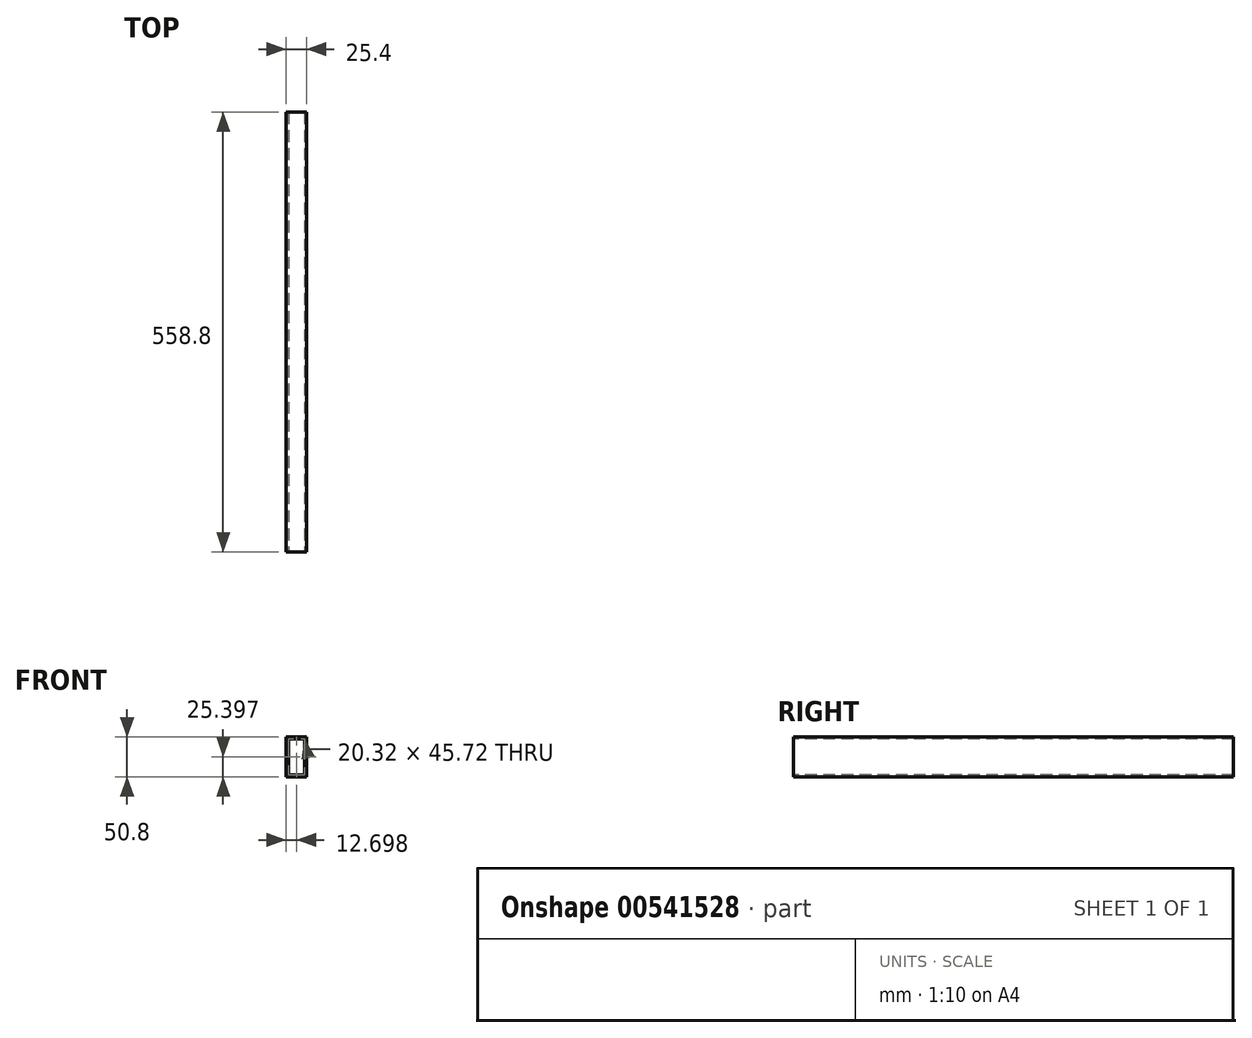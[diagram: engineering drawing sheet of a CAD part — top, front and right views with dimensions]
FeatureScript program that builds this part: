
annotation { "Feature Type Name" : "Feature", "Feature Type Description" : "" }
export const myFeature = defineFeature(function(context is Context, id is Id, definition is map)
    precondition{}
    {
        {
            var Q0;
            Q0=qCreatedBy(makeId("Front.planeOp"),FACE);
            var sketch = newSketch(context, id + "F0", { "sketchPlane" : qUnion([Q0])});
            skLineSegment(sketch, "E0.bottom", {"start": v(-22.94, 30.43) * mm, "end": v(2.46, 30.43) * mm});
            skLineSegment(sketch, "E0.top", {"start": v(-22.94, -20.37) * mm, "end": v(2.46, -20.37) * mm});
            skLineSegment(sketch, "E0.left", {"start": v(-22.94, 30.43) * mm, "end": v(-22.94, -20.37) * mm});
            skLineSegment(sketch, "E0.right", {"start": v(2.46, 30.43) * mm, "end": v(2.46, -20.37) * mm});
            skSolve(sketch);
        }
        {
            var Q0;
            Q0=qSketchRegion(id+"F0",true);
            extrude(context, id + "F1", {"entities" : qUnion([Q0]), "depth" : 558.8 * mm, "offsetDistance" : 25.4 * mm});
        }
        {
            var Q0;
            Q0=makeQuery(id+"F1.opExtrude","CAP_FACE",FACE,{"disambiguationData":[OSD([sQuery(id+"F0.wireOp",EDGE,"E0.bottom"),sQuery(id+"F0.wireOp",EDGE,"E0.top"),sQuery(id+"F0.wireOp",EDGE,"E0.left"),sQuery(id+"F0.wireOp",EDGE,"E0.right")])],"isStart":false});
            var sketch = newSketch(context, id + "F2", { "sketchPlane" : qUnion([Q0])});
            skLineSegment(sketch, "E1.bottom", {"start": v(-20.4, 27.89) * mm, "end": v(-0.08, 27.89) * mm});
            skLineSegment(sketch, "E1.top", {"start": v(-20.4, -17.83) * mm, "end": v(-0.08, -17.83) * mm});
            skLineSegment(sketch, "E1.left", {"start": v(-20.4, 27.89) * mm, "end": v(-20.4, -17.83) * mm});
            skLineSegment(sketch, "E1.right", {"start": v(-0.08, 27.89) * mm, "end": v(-0.08, -17.83) * mm});
            skSolve(sketch);
        }
        {
            var Q0;
            Q0=qSketchRegion(id+"F2",true);
            extrude(context, id + "F3", {"entities" : qUnion([Q0]), "operationType" : NewBodyOperationType.REMOVE, "endBound" : BoundingType.THROUGH_ALL, "oppositeDirection" : true, "depth" : 25.4 * mm, "offsetDistance" : 25.4 * mm});
        }
    });
